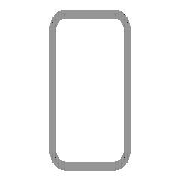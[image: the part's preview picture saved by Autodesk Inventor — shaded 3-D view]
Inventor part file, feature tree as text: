
AUTODESK INVENTOR PART (.ipt)
format: ipt  version: 2025 (Build 290162010, 162A)  size: 135,168 bytes
history: native  units: mm (DEFAULTED — no unit token found)
features: other x4, sketch x1, plane x1
ambient origin geometry x8: Origin, YZ Plane, XZ Plane, XY Plane, X Axis, Y Axis, Z Axis, Center Point
bodies: Solid1 (feature_tree), Body (feature_tree)
feature tree (6):
  parser-record x1  (decoder bookkeeping rows leaked as tree rows — omitted from the tree; the rows remain in map.json)
  other  "Driven Length"
  other  "Start Plane"
  other  "End Plane"
  sketch  "Sketch3"  dims[d3=760.0mm d4=0.0mm d7=6.0mm d9=20.0mm d11=40.0mm d12=3.0mm d13=20.0mm d14=780.0mm d15=10.0mm d16=20.0mm d17=90.0deg d18=760.0mm]
  plane  "Work Plane3"
